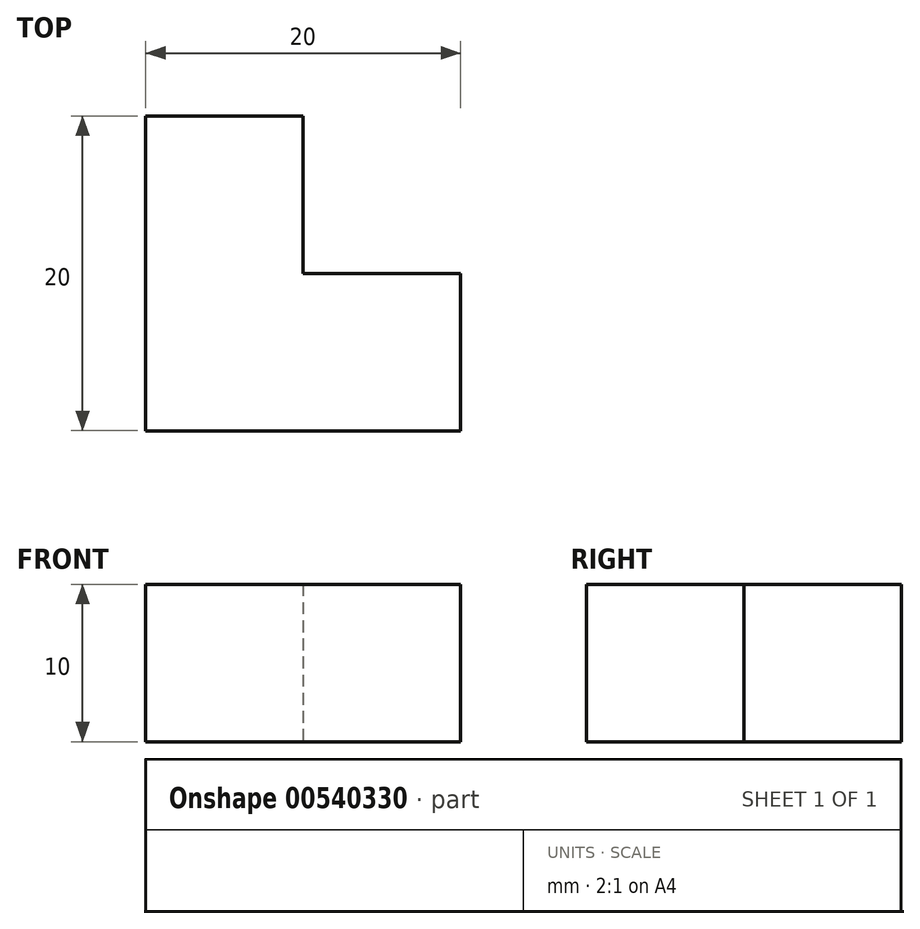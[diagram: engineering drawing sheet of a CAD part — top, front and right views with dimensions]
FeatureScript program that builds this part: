
annotation { "Feature Type Name" : "Feature", "Feature Type Description" : "" }
export const myFeature = defineFeature(function(context is Context, id is Id, definition is map)
    precondition{}
    {
        {
            var Q0;
            Q0=qCreatedBy(makeId("Top.planeOp"),FACE);
            var sketch = newSketch(context, id + "F0", { "sketchPlane" : qUnion([Q0])});
            skLineSegment(sketch, "E0", {"start": v(-26.04, 24.66) * mm, "end": v(-26.04, 4.66) * mm});
            skLineSegment(sketch, "E1", {"start": v(-16.04, 24.66) * mm, "end": v(-16.04, 14.66) * mm});
            skLineSegment(sketch, "E2", {"start": v(-16.04, 14.66) * mm, "end": v(-6.04, 14.66) * mm});
            skLineSegment(sketch, "E3", {"start": v(-6.04, 14.66) * mm, "end": v(-6.04, 4.66) * mm});
            skLineSegment(sketch, "E4", {"start": v(-26.04, 4.66) * mm, "end": v(-6.04, 4.66) * mm});
            skLineSegment(sketch, "E5", {"start": v(-26.04, 24.66) * mm, "end": v(-16.04, 24.66) * mm});
            skSolve(sketch);
        }
        {
            var Q0;
            Q0 = qSketchRegion(id + "F0", true);
            extrude(context, id + "F1", {"entities" : qUnion([Q0]), "depth" : 10 * mm, "offsetDistance" : 25 * mm});
        }
    });
